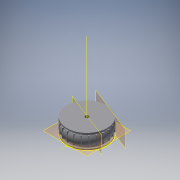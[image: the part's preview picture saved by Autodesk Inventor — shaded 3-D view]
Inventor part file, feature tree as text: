
AUTODESK INVENTOR PART (.ipt)
format: ipt  version: 2017 (Build 210142000, 142)  size: 516,608 bytes
history: native  units: mm
features: sketch x10, other x4, plane x4
ambient origin geometry x8: Origin, YZ Plane, XZ Plane, XY Plane, X Axis, Y Axis, Z Axis, Center Point
bodies: Solid1 (feature_tree)
feature tree (18):
  other  "front-wheel.ipt"
  other  "Solid1::front-wheel.ipt"
  other  "TaggingFeature1"
  sketch  "Sketch1"  dims[d0=10.0mm]
  sketch  "Sketch2"
  sketch  "Sketch3"
  sketch  "Sketch5"
  sketch  "Sketch6"
  sketch  "Sketch7"
  sketch  "Sketch8"
  sketch  "Sketch9"
  sketch  "Sketch14"
  sketch  "Sketch15"
  plane  "Work Plane1"
  plane  "Work Plane2"
  plane  "Work Plane3"
  plane  "Work Plane4"
  other  "Work Axis1"
